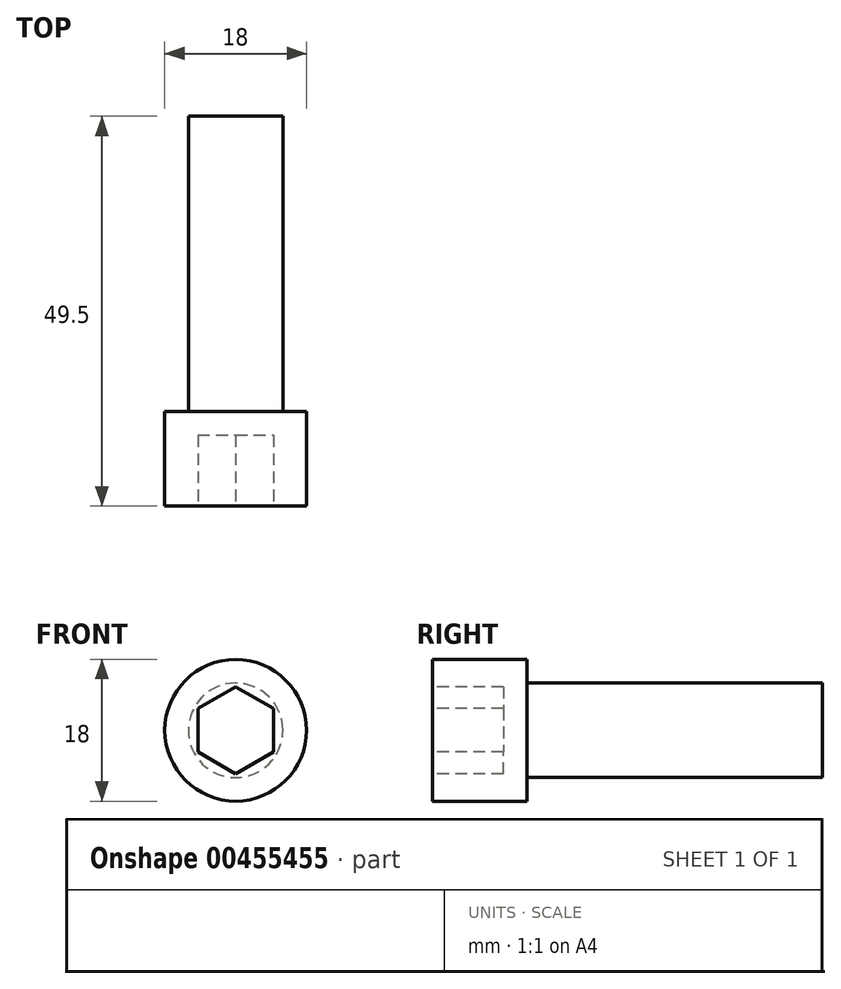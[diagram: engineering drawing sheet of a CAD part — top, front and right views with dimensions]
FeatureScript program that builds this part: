
annotation { "Feature Type Name" : "Feature", "Feature Type Description" : "" }
export const myFeature = defineFeature(function(context is Context, id is Id, definition is map)
    precondition{}
    {
        {
            var Q0;
            Q0=qCreatedBy(makeId("Front.planeOp"),FACE);
            var sketch = newSketch(context, id + "F0", { "sketchPlane" : qUnion([Q0])});
            skCircle(sketch, "E0", {"center": v(0, 0) * mm, "radius": 9 * mm});
            skSolve(sketch);
        }
        {
            var Q0;
            Q0 = qSketchRegion(id + "F0", true);
            extrude(context, id + "F1", {"entities" : qUnion([Q0]), "oppositeDirection" : true, "depth" : 12 * mm});
        }
        {
            var Q0;
            Q0=makeQuery(id+"F1.opExtrude","CAP_FACE",FACE,{"disambiguationData":[OSD([sQuery(id+"F0.wireOp",EDGE,"E0")])],"isStart":false});
            var sketch = newSketch(context, id + "F2", { "sketchPlane" : qUnion([Q0])});
            skCircle(sketch, "E1", {"center": v(0, 0) * mm, "radius": 6 * mm});
            skSolve(sketch);
        }
        {
            var Q0;
            Q0 = qSketchRegion(id + "F2", true);
            extrude(context, id + "F3", {"entities" : qUnion([Q0]), "operationType" : NewBodyOperationType.ADD, "depth" : 37.5 * mm});
        }
        {
            var Q0;
            Q0=makeQuery(id+"F1.opExtrude","CAP_FACE",FACE,{"disambiguationData":[OSD([sQuery(id+"F0.wireOp",EDGE,"E0")])],"isStart":true});
            var sketch = newSketch(context, id + "F4", { "sketchPlane" : qUnion([Q0])});
            skLineSegment(sketch, "E2.0", {"start": v(4.8, 2.77) * mm, "end": v(4.8, -2.77) * mm});
            skLineSegment(sketch, "E2.1", {"start": v(4.8, -2.77) * mm, "end": v(0, -5.54) * mm});
            skLineSegment(sketch, "E2.2", {"start": v(0, -5.54) * mm, "end": v(-4.8, -2.77) * mm});
            skLineSegment(sketch, "E2.3", {"start": v(-4.8, -2.77) * mm, "end": v(-4.8, 2.77) * mm});
            skLineSegment(sketch, "E2.4", {"start": v(-4.8, 2.77) * mm, "end": v(0, 5.54) * mm});
            skLineSegment(sketch, "E2.5", {"start": v(0, 5.54) * mm, "end": v(4.8, 2.77) * mm});
            skPoint(sketch, "E2.0.midPoint", {"position": v(4.8, 0) * mm});
            skLineSegment(sketch, "E3", {"start": v(0, 9.77) * mm, "end": v(0, -10.26) * mm, "construction": true});
            skCircle(sketch, "E4.0", {"center": v(0, 0) * mm, "radius": 9 * mm, "construction": true});
            skLineSegment(sketch, "E5", {"start": v(-10.58, 0) * mm, "end": v(16.79, 0) * mm, "construction": true});
            skSolve(sketch);
        }
        {
            var Q0;
            Q0 = qSketchRegion(id + "F4", true);
            extrude(context, id + "F5", {"entities" : qUnion([Q0]), "operationType" : NewBodyOperationType.REMOVE, "oppositeDirection" : true, "depth" : 9 * mm});
        }
    });
